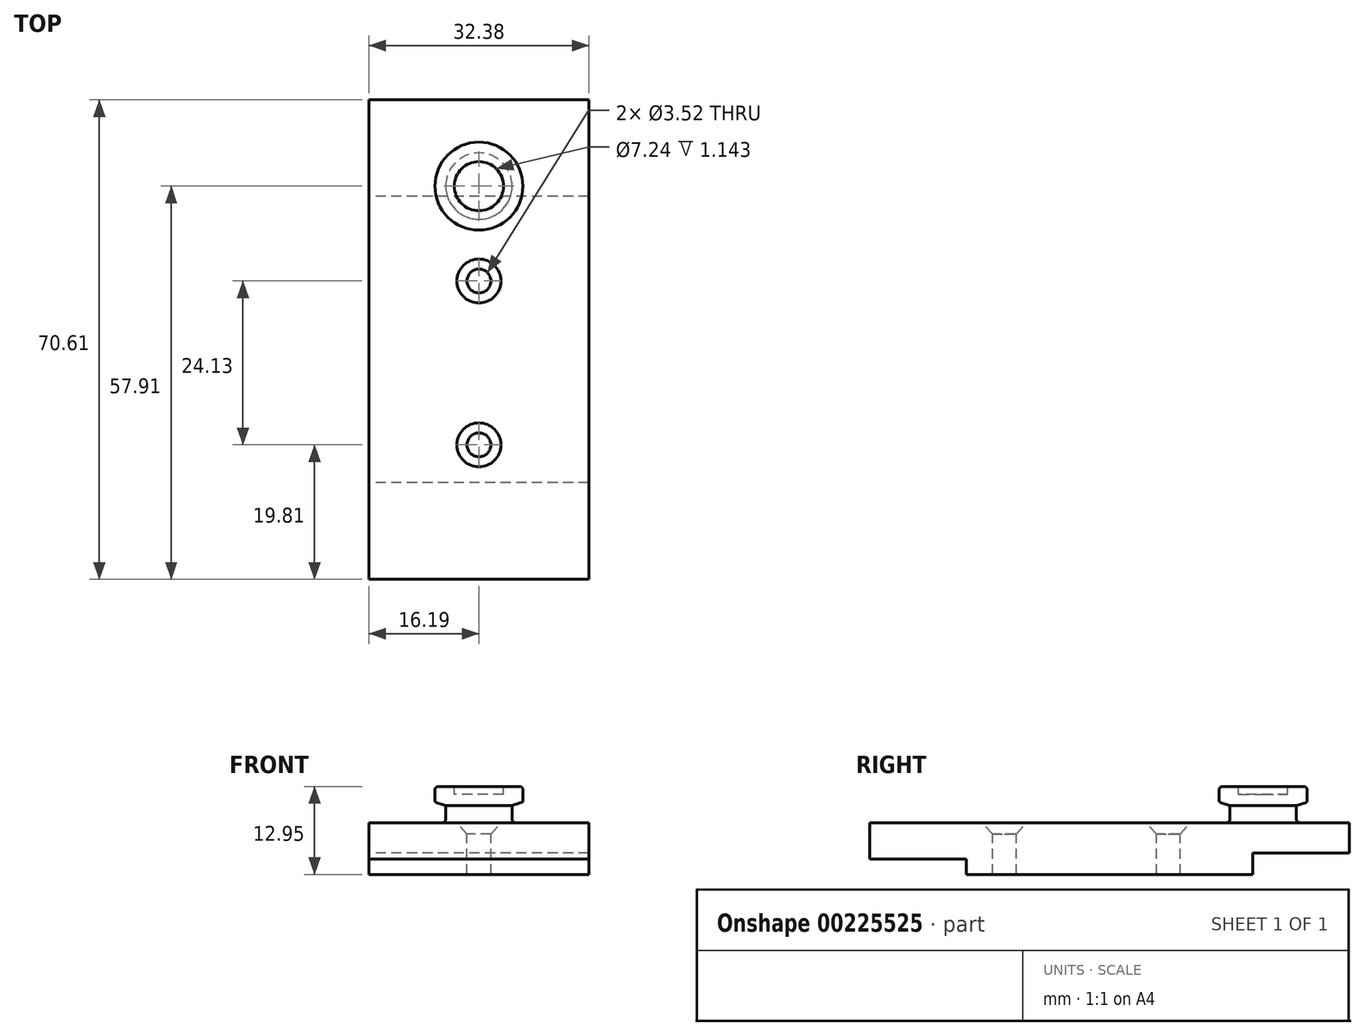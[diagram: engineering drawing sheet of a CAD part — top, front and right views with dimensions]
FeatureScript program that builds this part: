
annotation { "Feature Type Name" : "Feature", "Feature Type Description" : "" }
export const myFeature = defineFeature(function(context is Context, id is Id, definition is map)
    precondition{}
    {
        {
            var Q0;
            Q0=qCreatedBy(makeId("Front.planeOp"),FACE);
            var sketch = newSketch(context, id + "F0", { "sketchPlane" : qUnion([Q0])});
            skLineSegment(sketch, "E0", {"start": v(0, 0) * mm, "end": v(11.11, 0) * mm});
            skLineSegment(sketch, "E1", {"start": v(11.11, 0) * mm, "end": v(11.11, 5.08) * mm});
            skLineSegment(sketch, "E2", {"start": v(11.11, 5.08) * mm, "end": v(4.89, 5.08) * mm});
            skLineSegment(sketch, "E3", {"start": v(4.89, 5.08) * mm, "end": v(4.89, 7.62) * mm});
            skLineSegment(sketch, "E4", {"start": v(4.89, 7.62) * mm, "end": v(6.48, 7.62) * mm});
            skLineSegment(sketch, "E5", {"start": v(6.48, 7.62) * mm, "end": v(6.48, 10.41) * mm});
            skLineSegment(sketch, "E6", {"start": v(6.48, 10.41) * mm, "end": v(3.62, 10.41) * mm});
            skLineSegment(sketch, "E7", {"start": v(0, 10.41) * mm, "end": v(0, 0) * mm});
            skLineSegment(sketch, "E8", {"start": v(0, 9.27) * mm, "end": v(3.62, 9.27) * mm});
            skLineSegment(sketch, "E9", {"start": v(3.62, 9.27) * mm, "end": v(3.62, 10.41) * mm});
            skSolve(sketch);
        }
        {
            var Q0;
            Q0 = qSketchRegion(id + "F0", true);
            var Q1;
            Q1=sQuery(id+"F0.wireOp",EDGE,"E7");
            revolve(context, id + "F1", {"entities" : qUnion([Q0]), "axis" : qUnion([Q1]), "revolveType" : RevolveType.FULL});
        }
        {
            var Q0;
            Q0=makeQuery(id+"F1.opRevolve","SWEPT_EDGE",EDGE,{"disambiguationData":[OSD([sQuery(id+"F0.wireOp",EDGE,"E5"),sQuery(id+"F0.wireOp",EDGE,"E6")])]});
            var Q1;
            Q1=makeQuery(id+"F1.opRevolve","SWEPT_EDGE",EDGE,{"disambiguationData":[OSD([sQuery(id+"F0.wireOp",EDGE,"E2"),sQuery(id+"F0.wireOp",EDGE,"E3")])]});
            var Q2;
            Q2=makeQuery(id+"F1.opRevolve","SWEPT_EDGE",EDGE,{"disambiguationData":[OSD([sQuery(id+"F0.wireOp",EDGE,"E1"),sQuery(id+"F0.wireOp",EDGE,"E2")])]});
            fillet(context, id + "F2", {"entities" : qUnion([Q0, Q1, Q2]), "radius" : 0.5 * mm, "tangentPropagation" : true, "allowEdgeOverflow" : false});
        }
        {
            var Q0;
            Q0=makeQuery(id+"F1.opRevolve","SWEPT_EDGE",EDGE,{"disambiguationData":[OSD([sQuery(id+"F0.wireOp",EDGE,"E4"),sQuery(id+"F0.wireOp",EDGE,"E5")])]});
            chamfer(context, id + "F3", {"entities" : qUnion([Q0]), "chamferType" : ChamferType.OFFSET_ANGLE, "width" : 0.5 * mm, "oppositeDirection" : false, "angle" : 72.3 * degree, "tangentPropagation" : true});
        }
        {
            var Q0;
            {var subQ0=sQuery(id+"F0.wireOp",EDGE,"E5");Q0=makeQuery(id+"F3.opChamfer","BLEND_EDGE",EDGE,{"blendedFrom":[makeQuery(id+"F1.opRevolve","SWEPT_EDGE",EDGE,{"disambiguationData":[OSD([sQuery(id+"F0.wireOp",EDGE,"E4"),subQ0])]}),makeQuery(id+"F1.opRevolve","SWEPT_FACE",FACE,{"disambiguationData":[OSD([subQ0])]})],"blendedInto":[makeQuery(id+"F1.opRevolve","SWEPT_FACE",FACE,{"disambiguationData":[OSD([subQ0])]})]});}
            fillet(context, id + "F4", {"entities" : qUnion([Q0]), "radius" : 0.25 * mm, "tangentPropagation" : true, "allowEdgeOverflow" : false});
        }
        {
            var Q0;
            Q0=qCreatedBy(makeId("Right.planeOp"),FACE);
            var sketch = newSketch(context, id + "F5", { "sketchPlane" : qUnion([Q0])});
            skLineSegment(sketch, "E10.0", {"start": v(-10.6, 5.08) * mm, "end": v(10.6, 5.08) * mm, "construction": true});
            skLineSegment(sketch, "E11.top", {"start": v(12.7, 5.08) * mm, "end": v(-57.91, 5.08) * mm});
            skPoint(sketch, "E12", {"position": v(0, 5.08) * mm});
            skPoint(sketch, "E11.left.start.orphan", {"position": v(12.7, 0) * mm});
            skLineSegment(sketch, "E13.top", {"start": v(12.7, -2.54) * mm, "end": v(-57.91, -2.54) * mm});
            skLineSegment(sketch, "E13.left", {"start": v(12.7, 5.08) * mm, "end": v(12.7, -2.54) * mm});
            skLineSegment(sketch, "E13.right", {"start": v(-57.91, 5.08) * mm, "end": v(-57.91, -2.54) * mm});
            skSolve(sketch);
        }
        {
            var Q0;
            Q0 = qSketchRegion(id + "F5", true);
            extrude(context, id + "F6", {"entities" : qUnion([Q0]), "operationType" : NewBodyOperationType.ADD, "endBound" : BoundingType.SYMMETRIC, "depth" : 32.38 * mm});
        }
        {
            var Q0;
            Q0=makeQuery(id+"F6.opExtrude","CAP_FACE",FACE,{"disambiguationData":[OSD([sQuery(id+"F5.wireOp",EDGE,"E11.top"),sQuery(id+"F5.wireOp",EDGE,"E13.top"),sQuery(id+"F5.wireOp",EDGE,"E13.left"),sQuery(id+"F5.wireOp",EDGE,"E13.right")])],"isStart":true});
            var sketch = newSketch(context, id + "F7", { "sketchPlane" : qUnion([Q0])});
            skLineSegment(sketch, "E14", {"start": v(-12.7, 0.64) * mm, "end": v(1.52, 0.64) * mm});
            skLineSegment(sketch, "E15", {"start": v(1.52, 0.64) * mm, "end": v(1.52, -2.54) * mm});
            skLineSegment(sketch, "E16", {"start": v(1.52, -2.54) * mm, "end": v(-12.7, -2.54) * mm});
            skLineSegment(sketch, "E17", {"start": v(-12.7, -2.54) * mm, "end": v(-12.7, 0.64) * mm});
            skLineSegment(sketch, "E18.bottom", {"start": v(57.91, -2.54) * mm, "end": v(43.69, -2.54) * mm});
            skLineSegment(sketch, "E18.top", {"start": v(57.91, -0.25) * mm, "end": v(43.69, -0.25) * mm});
            skLineSegment(sketch, "E18.left", {"start": v(57.91, -2.54) * mm, "end": v(57.91, -0.25) * mm});
            skLineSegment(sketch, "E18.right", {"start": v(43.69, -2.54) * mm, "end": v(43.69, -0.25) * mm});
            skSolve(sketch);
        }
        {
            var Q0;
            Q0 = qSketchRegion(id + "F7", true);
            extrude(context, id + "F8", {"entities" : qUnion([Q0]), "operationType" : NewBodyOperationType.REMOVE, "endBound" : BoundingType.THROUGH_ALL, "oppositeDirection" : true, "depth" : 25.4 * mm});
        }
        {
            var Q0;
            Q0=makeQuery(id+"F6.boolean.opBoolean","MERGE",FACE,{"derivedFrom":[makeQuery(id+"F1.opRevolve","SWEPT_FACE",FACE,{"disambiguationData":[OSD([sQuery(id+"F0.wireOp",EDGE,"E2")])]}),makeQuery(id+"F6.opExtrude","SWEPT_FACE",FACE,{"disambiguationData":[OSD([sQuery(id+"F5.wireOp",EDGE,"E11.top")])]})]});
            var sketch = newSketch(context, id + "F9", { "sketchPlane" : qUnion([Q0])});
            skPoint(sketch, "E19", {"position": v(0, -13.97) * mm});
            skPoint(sketch, "E20", {"position": v(0, -38.1) * mm});
            skSolve(sketch);
        }
        {
            var Q0;
            Q0=sQuery(id+"F9.wireOp",VERTEX,"E19");
            var Q1;
            Q1=sQuery(id+"F9.wireOp",VERTEX,"E20");
            var Q2;
            Q2=makeQuery(id+"F1.opRevolve","SWEPT_BODY",BODY,{"disambiguationData":[OSD([sQuery(id+"F0.wireOp",EDGE,"E0"),sQuery(id+"F0.wireOp",EDGE,"E1"),sQuery(id+"F0.wireOp",EDGE,"E2"),sQuery(id+"F0.wireOp",EDGE,"E3"),sQuery(id+"F0.wireOp",EDGE,"E4"),sQuery(id+"F0.wireOp",EDGE,"E5"),sQuery(id+"F0.wireOp",EDGE,"E6"),sQuery(id+"F0.wireOp",EDGE,"E7"),sQuery(id+"F0.wireOp",EDGE,"E8"),sQuery(id+"F0.wireOp",EDGE,"E9")])]});
            hole(context, id + "F10", {"style" : HoleStyle.C_SINK, "endStyle" : HoleEndStyle.THROUGH, "holeDiameter" : 3.52 * mm, "cSinkDiameter" : 6.48 * mm, "cSinkAngle" : 82 * degree, "locations" : qUnion([Q0, Q1]), "scope" : qUnion([Q2]), "isTappedThrough" : true});
        }
    });
